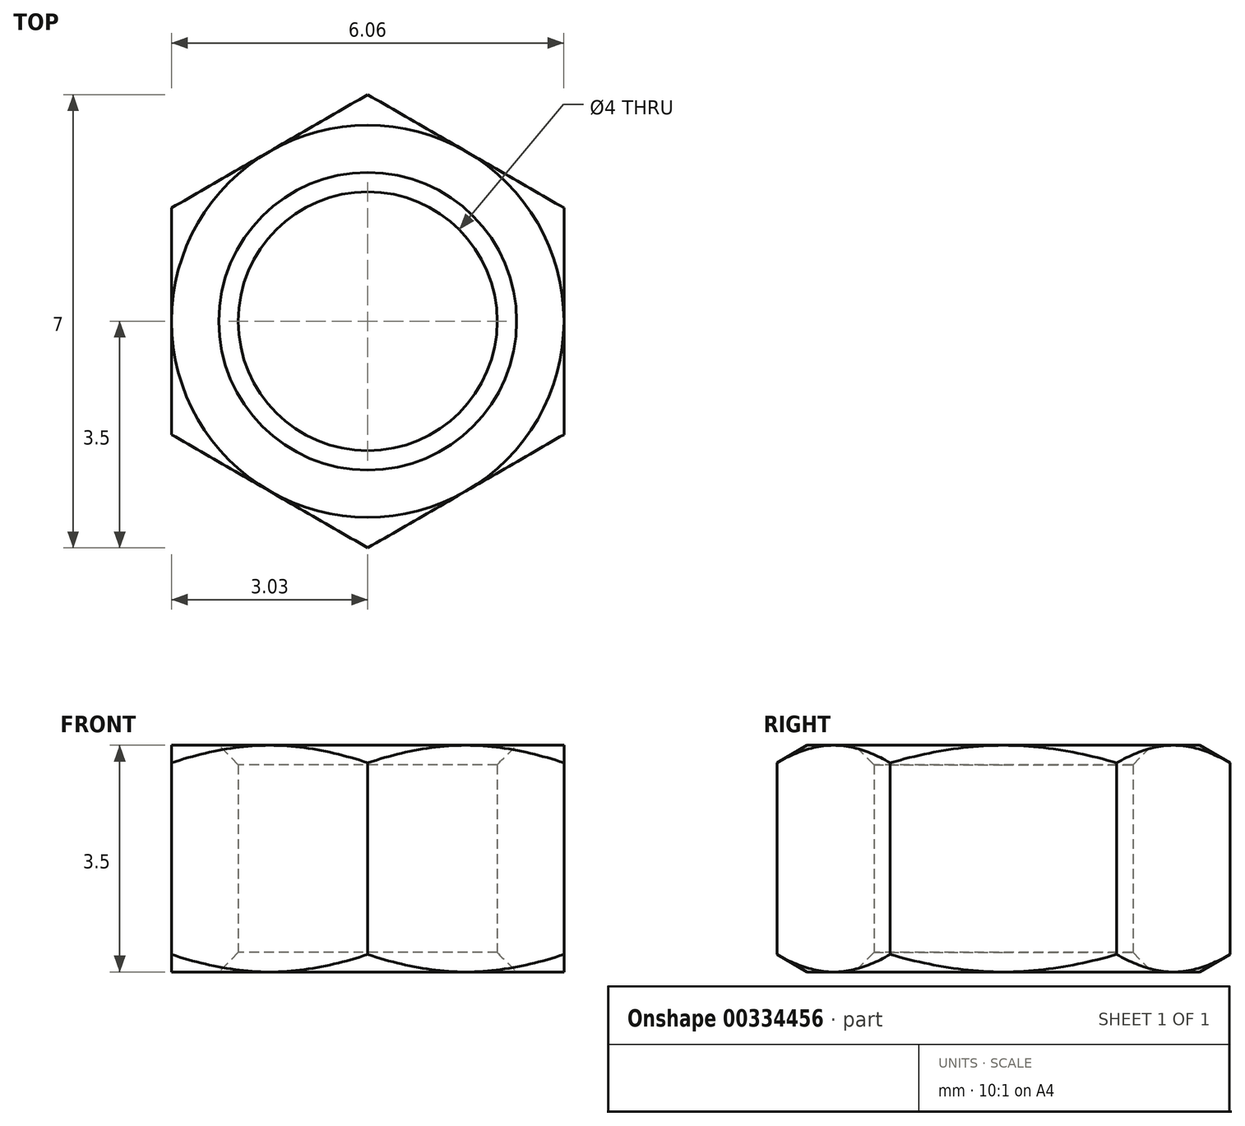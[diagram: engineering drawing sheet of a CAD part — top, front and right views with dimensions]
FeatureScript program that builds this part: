
annotation { "Feature Type Name" : "Feature", "Feature Type Description" : "" }
export const myFeature = defineFeature(function(context is Context, id is Id, definition is map)
    precondition{}
    {
        {
            var Q0;
            Q0=qCreatedBy(makeId("Top.planeOp"),FACE);
            var sketch = newSketch(context, id + "F0", { "sketchPlane" : qUnion([Q0])});
            skCircle(sketch, "E0.cCircle", {"center": v(0, 0) * mm, "radius": 3.5 * mm, "construction": true});
            skLineSegment(sketch, "E0.0", {"start": v(0, 3.5) * mm, "end": v(3.03, 1.75) * mm});
            skLineSegment(sketch, "E0.1", {"start": v(3.03, 1.75) * mm, "end": v(3.03, -1.75) * mm});
            skLineSegment(sketch, "E0.2", {"start": v(3.03, -1.75) * mm, "end": v(0, -3.5) * mm});
            skLineSegment(sketch, "E0.3", {"start": v(0, -3.5) * mm, "end": v(-3.03, -1.75) * mm});
            skLineSegment(sketch, "E0.4", {"start": v(-3.03, -1.75) * mm, "end": v(-3.03, 1.75) * mm});
            skLineSegment(sketch, "E0.5", {"start": v(-3.03, 1.75) * mm, "end": v(0, 3.5) * mm});
            skCircle(sketch, "E1", {"center": v(0, 0) * mm, "radius": 2 * mm});
            skSolve(sketch);
        }
        {
            var Q0;
            Q0=makeQuery(id+"F0.imprint","IMPRINT",FACE,{"disambiguationData":[TD([[makeQuery(id+"F0.imprint","IMPRINT",EDGE,{"derivedFrom":sQuery(id+"F0.wireOp",EDGE,"E0.0")}),-1.0]])]});
            extrude(context, id + "F1", {"entities" : qUnion([Q0]), "depth" : 3.5 * mm});
        }
        {
            var Q0;
            Q0=qCreatedBy(makeId("Front.planeOp"),FACE);
            var sketch = newSketch(context, id + "F2", { "sketchPlane" : qUnion([Q0])});
            skLineSegment(sketch, "E2", {"start": v(0, 3.5) * mm, "end": v(0, 0) * mm, "construction": true});
            skLineSegment(sketch, "E3", {"start": v(0, 1.75) * mm, "end": v(3.03, 1.75) * mm, "construction": true});
            skLineSegment(sketch, "E4", {"start": v(3.03, 0) * mm, "end": v(5.8, 0) * mm});
            skLineSegment(sketch, "E5", {"start": v(5.8, 0) * mm, "end": v(5.8, 1.6) * mm});
            skLineSegment(sketch, "E6", {"start": v(5.8, 1.6) * mm, "end": v(3.03, 0) * mm});
            skLineSegment(sketch, "E7.MirrorCS", {"start": v(5.8, 1.9) * mm, "end": v(3.03, 3.5) * mm});
            skLineSegment(sketch, "E8.MirrorCS", {"start": v(5.8, 3.5) * mm, "end": v(5.8, 1.9) * mm});
            skLineSegment(sketch, "E9.MirrorCS", {"start": v(3.03, 3.5) * mm, "end": v(5.8, 3.5) * mm});
            skSolve(sketch);
        }
        {
            var Q0;
            Q0=makeQuery(id+"F2.imprint","IMPRINT",FACE,{"disambiguationData":[TD([[makeQuery(id+"F2.imprint","IMPRINT",EDGE,{"derivedFrom":sQuery(id+"F2.wireOp",EDGE,"E7.MirrorCS")}),-1.0]])]});
            var Q1;
            Q1=makeQuery(id+"F2.imprint","IMPRINT",FACE,{"disambiguationData":[TD([[makeQuery(id+"F2.imprint","IMPRINT",EDGE,{"derivedFrom":sQuery(id+"F2.wireOp",EDGE,"E4")}),1.0]])]});
            var Q2;
            Q2=sQuery(id+"F2.wireOp",EDGE,"E2");
            revolve(context, id + "F3", {"operationType" : NewBodyOperationType.REMOVE, "entities" : qUnion([Q0, Q1]), "axis" : qUnion([Q2]), "revolveType" : RevolveType.FULL, "oppositeDirection" : true});
        }
        {
            var Q0;
            Q0=makeQuery(id+"F1.opExtrude","CAP_EDGE",EDGE,{"disambiguationData":[OSD([sQuery(id+"F0.wireOp",EDGE,"E1")])],"isStart":false});
            var Q1;
            Q1=makeQuery(id+"F1.opExtrude","CAP_EDGE",EDGE,{"disambiguationData":[OSD([sQuery(id+"F0.wireOp",EDGE,"E1")])],"isStart":true});
            chamfer(context, id + "F4", {"entities" : qUnion([Q0, Q1]), "width" : 0.3 * mm, "tangentPropagation" : true});
        }
    });
